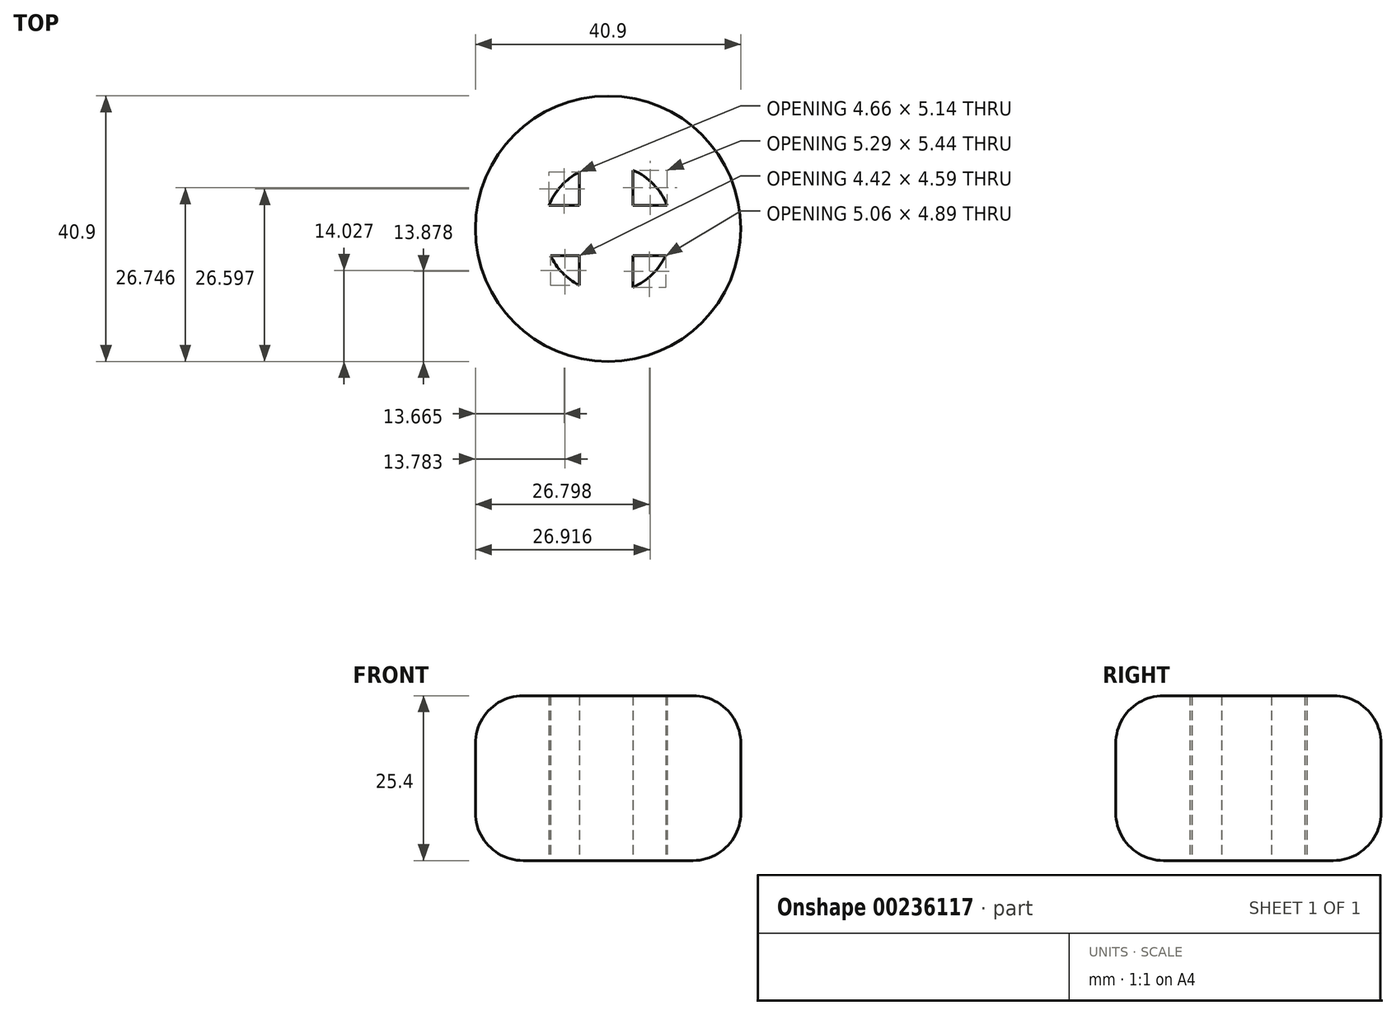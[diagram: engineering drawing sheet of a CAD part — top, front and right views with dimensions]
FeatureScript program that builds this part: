
annotation { "Feature Type Name" : "Feature", "Feature Type Description" : "" }
export const myFeature = defineFeature(function(context is Context, id is Id, definition is map)
    precondition{}
    {
        {
            var Q0;
            Q0=qCreatedBy(makeId("Top.planeOp"),FACE);
            var sketch = newSketch(context, id + "F0", { "sketchPlane" : qUnion([Q0])});
            skArc(sketch, "E0", {"start": v(-4.46, 8.72) * mm, "mid": v(-7.26, 6.57) * mm, "end": v(-9.11, 3.58) * mm});
            skCircle(sketch, "E1", {"center": v(0, 0) * mm, "radius": 20.45 * mm});
            skLineSegment(sketch, "E2", {"start": v(-4.46, 19.96) * mm, "end": v(-4.46, 3.58) * mm});
            skLineSegment(sketch, "E3", {"start": v(3.82, 20.09) * mm, "end": v(3.82, 3.58) * mm});
            skLineSegment(sketch, "E4", {"start": v(-20.13, 3.58) * mm, "end": v(-4.46, 3.58) * mm});
            skLineSegment(sketch, "E5", {"start": v(-20.03, -4.13) * mm, "end": v(-4.46, -4.13) * mm});
            skArc(sketch, "E6.trimOffspring", {"start": v(3.82, -9.01) * mm, "mid": v(6.8, -7.04) * mm, "end": v(8.88, -4.13) * mm});
            skArc(sketch, "E7.trimOffspring", {"start": v(9.11, 3.58) * mm, "mid": v(7.01, 6.83) * mm, "end": v(3.82, 9.01) * mm});
            skLineSegment(sketch, "E8.trimOffspring", {"start": v(3.82, -4.13) * mm, "end": v(3.82, -20.09) * mm});
            skLineSegment(sketch, "E9.trimOffspring", {"start": v(-4.46, -4.13) * mm, "end": v(-4.46, -19.96) * mm});
            skLineSegment(sketch, "E10.trimOffspring", {"start": v(3.82, 3.58) * mm, "end": v(20.13, 3.58) * mm});
            skLineSegment(sketch, "E11.trimOffspring", {"start": v(3.82, -4.13) * mm, "end": v(20.03, -4.13) * mm});
            skArc(sketch, "E12.trimOffspring", {"start": v(-8.88, -4.13) * mm, "mid": v(-7.05, -6.8) * mm, "end": v(-4.46, -8.72) * mm});
            skSolve(sketch);
        }
        {
            var Q0;
            Q0 = qSketchRegion(id + "F0", true);
            extrude(context, id + "F1", {"entities" : qUnion([Q0]), "endBound" : BoundingType.SYMMETRIC, "depth" : 25.4 * mm});
        }
        {
            var Q0;
            Q0=makeQuery(id+"F1.opExtrude","CAP_EDGE",EDGE,{"disambiguationData":[OSD([sQuery(id+"F0.wireOp",EDGE,"E1")])],"isStart":false});
            var Q1;
            Q1=makeQuery(id+"F1.opExtrude","CAP_EDGE",EDGE,{"disambiguationData":[OSD([sQuery(id+"F0.wireOp",EDGE,"E1")])],"isStart":true});
            fillet(context, id + "F2", {"entities" : qUnion([Q0, Q1]), "radius" : 7.36 * mm, "tangentPropagation" : true, "allowEdgeOverflow" : false});
        }
    });
